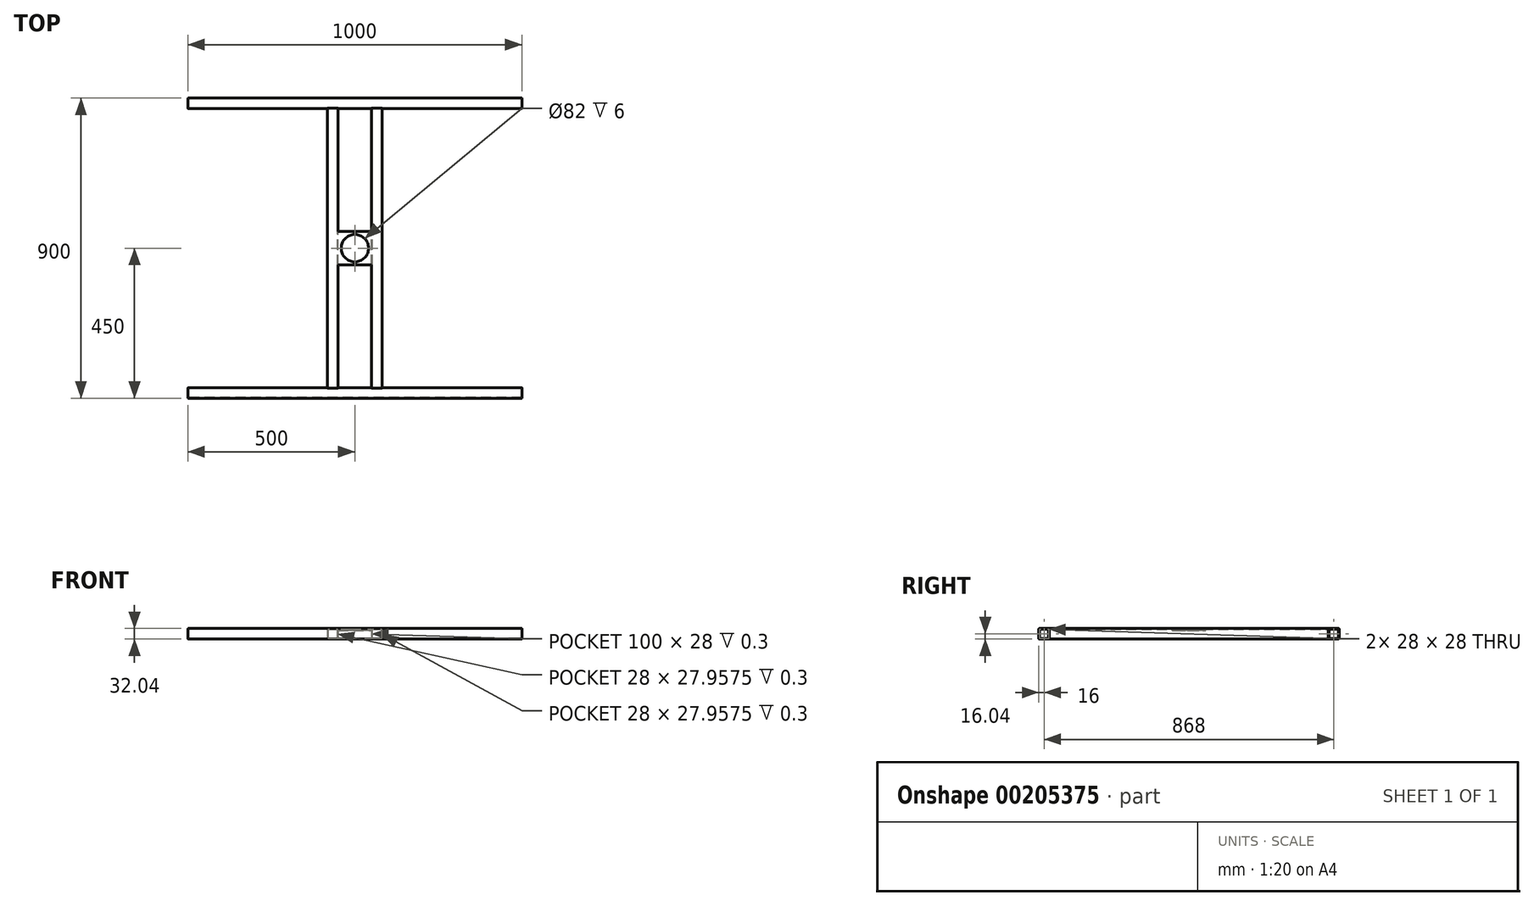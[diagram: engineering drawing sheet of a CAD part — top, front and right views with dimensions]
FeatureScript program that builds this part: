
annotation { "Feature Type Name" : "Feature", "Feature Type Description" : "" }
export const myFeature = defineFeature(function(context is Context, id is Id, definition is map)
    precondition{}
    {
        {
            var Q0;
            Q0=qCreatedBy(makeId("Right.planeOp"),FACE);
            var sketch = newSketch(context, id + "F0", { "sketchPlane" : qUnion([Q0])});
            skLineSegment(sketch, "E0.bottom", {"start": v(-448, -16) * mm, "end": v(-420, -16) * mm});
            skLineSegment(sketch, "E0.top", {"start": v(-448, 16) * mm, "end": v(-420, 16) * mm});
            skLineSegment(sketch, "E0.left", {"start": v(-450, -14) * mm, "end": v(-450, 14) * mm});
            skLineSegment(sketch, "E0.right", {"start": v(-418, -14) * mm, "end": v(-418, 14) * mm});
            skPoint(sketch, "E0.middle", {"position": v(-434, 0) * mm});
            skLineSegment(sketch, "E1.bottom", {"start": v(-448, 14) * mm, "end": v(-420, 14) * mm});
            skLineSegment(sketch, "E1.top", {"start": v(-448, -14) * mm, "end": v(-420, -14) * mm});
            skLineSegment(sketch, "E1.left", {"start": v(-448, 14) * mm, "end": v(-448, -14) * mm});
            skLineSegment(sketch, "E1.right", {"start": v(-420, 14) * mm, "end": v(-420, -14) * mm});
            skPoint(sketch, "E2.visualSharp", {"position": v(-450, 16) * mm});
            skArc(sketch, "E2.filletArc", {"start": v(-448, 16) * mm, "mid": v(-449.41, 15.41) * mm, "end": v(-450, 14) * mm});
            skPoint(sketch, "E3.visualSharp", {"position": v(-450, -16) * mm});
            skArc(sketch, "E3.filletArc", {"start": v(-450, -14) * mm, "mid": v(-449.41, -15.41) * mm, "end": v(-448, -16) * mm});
            skPoint(sketch, "E4.visualSharp", {"position": v(-418, -16) * mm});
            skArc(sketch, "E4.filletArc", {"start": v(-420, -16) * mm, "mid": v(-418.59, -15.41) * mm, "end": v(-418, -14) * mm});
            skPoint(sketch, "E5.visualSharp", {"position": v(-418, 16) * mm});
            skArc(sketch, "E5.filletArc", {"start": v(-418, 14) * mm, "mid": v(-418.59, 15.41) * mm, "end": v(-420, 16) * mm});
            skArc(sketch, "E6.MirrorCS", {"start": v(448, 16) * mm, "mid": v(449.41, 15.41) * mm, "end": v(450, 14) * mm});
            skArc(sketch, "E7.MirrorCS", {"start": v(450, -14) * mm, "mid": v(449.41, -15.41) * mm, "end": v(448, -16) * mm});
            skArc(sketch, "E8.MirrorCS", {"start": v(420, -16) * mm, "mid": v(418.59, -15.41) * mm, "end": v(418, -14) * mm});
            skArc(sketch, "E9.MirrorCS", {"start": v(418, 14) * mm, "mid": v(418.59, 15.41) * mm, "end": v(420, 16) * mm});
            skPoint(sketch, "E10.MirrorP", {"position": v(434, 0) * mm});
            skPoint(sketch, "E11.MirrorP", {"position": v(450, -16) * mm});
            skLineSegment(sketch, "E12.MirrorCS", {"start": v(448, -16) * mm, "end": v(420, -16) * mm});
            skLineSegment(sketch, "E13.MirrorCS", {"start": v(448, 16) * mm, "end": v(420, 16) * mm});
            skLineSegment(sketch, "E14.MirrorCS", {"start": v(450, -14) * mm, "end": v(450, 14) * mm});
            skLineSegment(sketch, "E15.MirrorCS", {"start": v(418, -14) * mm, "end": v(418, 14) * mm});
            skLineSegment(sketch, "E16.MirrorCS", {"start": v(448, 14) * mm, "end": v(420, 14) * mm});
            skLineSegment(sketch, "E17.MirrorCS", {"start": v(448, -14) * mm, "end": v(420, -14) * mm});
            skPoint(sketch, "E18.MirrorP", {"position": v(418, 16) * mm});
            skLineSegment(sketch, "E19.MirrorCS", {"start": v(448, 14) * mm, "end": v(448, -14) * mm});
            skPoint(sketch, "E20.MirrorP", {"position": v(450, 16) * mm});
            skLineSegment(sketch, "E21.MirrorCS", {"start": v(420, 14) * mm, "end": v(420, -14) * mm});
            skPoint(sketch, "E22.MirrorP", {"position": v(418, -16) * mm});
            skSolve(sketch);
        }
        {
            var Q0;
            Q0 = qSketchRegion(id + "F0", true);
            extrude(context, id + "F1", {"entities" : qUnion([Q0]), "endBound" : BoundingType.SYMMETRIC, "depth" : 1000 * mm});
        }
        {
            var Q0;
            Q0=qCreatedBy(makeId("Front.planeOp"),FACE);
            var sketch = newSketch(context, id + "F2", { "sketchPlane" : qUnion([Q0])});
            skLineSegment(sketch, "E23.bottom", {"start": v(-50, -50) * mm, "end": v(50, -50) * mm, "construction": true});
            skLineSegment(sketch, "E23.top", {"start": v(-50, 50) * mm, "end": v(50, 50) * mm, "construction": true});
            skLineSegment(sketch, "E23.right", {"start": v(50, -50) * mm, "end": v(50, 50) * mm, "construction": true});
            skPoint(sketch, "E23.middle", {"position": v(0, 0) * mm});
            skLineSegment(sketch, "E24.bottom", {"start": v(-50, -16.04) * mm, "end": v(-82, -16.04) * mm});
            skLineSegment(sketch, "E24.top", {"start": v(-50, 15.96) * mm, "end": v(-82, 15.96) * mm});
            skLineSegment(sketch, "E24.left", {"start": v(-50, -16.04) * mm, "end": v(-50, 15.96) * mm});
            skLineSegment(sketch, "E24.right", {"start": v(-82, -16.04) * mm, "end": v(-82, 15.96) * mm});
            skLineSegment(sketch, "E25.MirrorCS", {"start": v(82, -16.04) * mm, "end": v(82, 15.96) * mm});
            skLineSegment(sketch, "E26.MirrorCS", {"start": v(50, -16.04) * mm, "end": v(82, -16.04) * mm});
            skLineSegment(sketch, "E27.MirrorCS", {"start": v(50, 15.96) * mm, "end": v(82, 15.96) * mm});
            skLineSegment(sketch, "E28.MirrorCS", {"start": v(50, -16.04) * mm, "end": v(50, 15.96) * mm});
            skLineSegment(sketch, "E29.0", {"start": v(-52, -14.04) * mm, "end": v(-52, 13.96) * mm});
            skLineSegment(sketch, "E29.1", {"start": v(-52, -14.04) * mm, "end": v(-80, -14.04) * mm});
            skLineSegment(sketch, "E29.2", {"start": v(-80, -14.04) * mm, "end": v(-80, 13.96) * mm});
            skLineSegment(sketch, "E29.3", {"start": v(-52, 13.96) * mm, "end": v(-80, 13.96) * mm});
            skLineSegment(sketch, "E30.MirrorCS", {"start": v(52, -14.04) * mm, "end": v(52, 13.96) * mm});
            skLineSegment(sketch, "E31.MirrorCS", {"start": v(80, -14.04) * mm, "end": v(80, 13.96) * mm});
            skLineSegment(sketch, "E32.MirrorCS", {"start": v(52, 13.96) * mm, "end": v(80, 13.96) * mm});
            skLineSegment(sketch, "E33.MirrorCS", {"start": v(52, -14.04) * mm, "end": v(80, -14.04) * mm});
            skSolve(sketch);
        }
        {
            var Q0;
            Q0=makeQuery(id+"F2.imprint","IMPRINT",FACE,{"disambiguationData":[TD([[makeQuery(id+"F2.imprint","IMPRINT",EDGE,{"derivedFrom":sQuery(id+"F2.wireOp",EDGE,"E24.bottom")}),-1.0]])]});
            var Q1;
            Q1=makeQuery(id+"F2.imprint","IMPRINT",FACE,{"disambiguationData":[TD([[makeQuery(id+"F2.imprint","IMPRINT",EDGE,{"derivedFrom":sQuery(id+"F2.wireOp",EDGE,"E28.MirrorCS")}),-1.0]])]});
            extrude(context, id + "F3", {"entities" : qUnion([Q0, Q1]), "operationType" : NewBodyOperationType.ADD, "endBound" : BoundingType.SYMMETRIC, "depth" : 840.6 * mm});
        }
        {
            var Q0;
            Q0=makeQuery(id+"F3.opExtrude","SWEPT_FACE",FACE,{"disambiguationData":[OSD([sQuery(id+"F2.wireOp",EDGE,"E24.top")])]});
            var sketch = newSketch(context, id + "F4", { "sketchPlane" : qUnion([Q0])});
            skLineSegment(sketch, "E34.bottom", {"start": v(-50, -50) * mm, "end": v(50, -50) * mm});
            skLineSegment(sketch, "E34.top", {"start": v(-50, 50) * mm, "end": v(50, 50) * mm});
            skLineSegment(sketch, "E34.left", {"start": v(-50, -50) * mm, "end": v(-50, 50) * mm});
            skLineSegment(sketch, "E34.right", {"start": v(50, -50) * mm, "end": v(50, 50) * mm});
            skPoint(sketch, "E34.middle", {"position": v(0, 0) * mm});
            skSolve(sketch);
        }
        {
            var Q0;
            Q0=makeQuery(id+"F4.imprint","IMPRINT",FACE,{"disambiguationData":[TD([[makeQuery(id+"F4.imprint","IMPRINT",EDGE,{"derivedFrom":sQuery(id+"F4.wireOp",EDGE,"E34.bottom")}),1.0]])]});
            extrude(context, id + "F5", {"entities" : qUnion([Q0]), "operationType" : NewBodyOperationType.ADD, "oppositeDirection" : true, "depth" : 6 * mm});
        }
        {
            var Q0;
            Q0=makeQuery(id+"F5.boolean.opBoolean","MERGE",FACE,{"derivedFrom":[makeQuery(id+"F3.opExtrude","SWEPT_FACE",FACE,{"disambiguationData":[OSD([sQuery(id+"F2.wireOp",EDGE,"E24.top")])]}),makeQuery(id+"F3.opExtrude","SWEPT_FACE",FACE,{"disambiguationData":[OSD([sQuery(id+"F2.wireOp",EDGE,"E27.MirrorCS")])]}),makeQuery(id+"F5.opExtrude","CAP_FACE",FACE,{"disambiguationData":[OSD([sQuery(id+"F4.wireOp",EDGE,"E34.bottom"),sQuery(id+"F4.wireOp",EDGE,"E34.top"),sQuery(id+"F4.wireOp",EDGE,"E34.left"),sQuery(id+"F4.wireOp",EDGE,"E34.right")])],"isStart":true})]});
            var sketch = newSketch(context, id + "F6", { "sketchPlane" : qUnion([Q0])});
            skCircle(sketch, "E35", {"center": v(0, 0) * mm, "radius": 41 * mm});
            skSolve(sketch);
        }
        {
            var Q0;
            Q0 = qSketchRegion(id + "F6", true);
            extrude(context, id + "F7", {"entities" : qUnion([Q0]), "operationType" : NewBodyOperationType.REMOVE, "oppositeDirection" : true, "depth" : 25 * mm});
        }
    });
